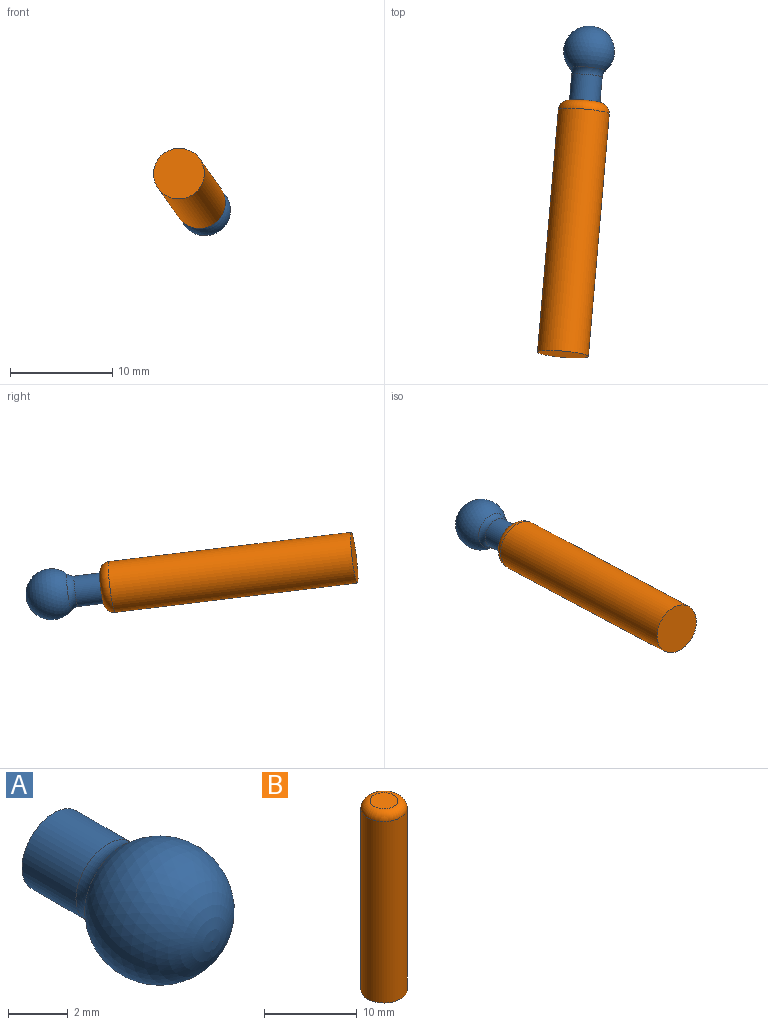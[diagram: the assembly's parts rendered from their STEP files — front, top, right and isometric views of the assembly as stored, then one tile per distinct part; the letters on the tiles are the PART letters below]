
ASSEMBLY  parts=2 mates=1
PART A: 4 faces, bbox 5x7.5x5 mm
  f0: sphere r=2.5mm, area 66.8mm2, adj f3
  f1: cylinder r=1.5mm len=3mm, axis (0,-1,0), area 24mm2, adj f2,f3
  f2: plane 3x3mm, normal (0,1,0), area 7.1mm2, adj f1
  f3: torus R=2.5mm, axis (0,-1,0), area 7.8mm2, adj f0,f1
PART B: 4 faces, bbox 5.4x5.4x25 mm
  f0: cylinder r=2.5mm len=24mm, axis (0,0,-1), area 377mm2, adj f2,f3
  f1: plane 3x3mm, normal (0,0,1), area 7.1mm2, adj f3
  f2: plane 5x5mm, normal (0,0,-1), area 19.6mm2, adj f0
  f3: torus R=1.5mm, axis (0,0,1), area 21.1mm2, adj f0,f1
PLACE A rot(axis=(1,-0.04,0.01),173.1deg) t=(2.77,32.15,-3.89)mm
PLACE B rot(axis=(-1,0.03,-0.05),97.1deg) t=(-1.07,-12.36,1.5)mm fixed
MATE fastened A.f1 <-> B.f0  axis (-0.09,-0.99,0.12) through (2.35,27.2,-3.29)mm
